# Revit family: Запорно-регулирующая заслонка с рукояткой AF-4219
name_source: partatom
category: Rohrzubehör
units: mm (PartAtom-declared; Revit-internal decimal feet)

## family parameters
Arbeitsebenenbasiert = Nein
Beim Laden mit Abzugskörper schneiden = Nein
Bemaßung runder Anschluss = Durchmesser verwenden
Gemeinsam genutzt = Nein
Immer vertikal = Ja
OmniClass-Nummer = 23.65.55.14
OmniClass-Titel = Valves for Liquid Services
Teiletyp = Unterbricht

## types (1)
- Запорно-регулирующая заслонка с рукояткой AF-4219
    Hersteller = HERZ Armaturen Ges.m.b.H.
    O-Ring = EPDM в соответствии с ISO 1691
    R99 = 2 mm  [stored 0.00656168 ft]
    SCRNCODE = 05;13;02
    SCRNSEQ = ARM;AM_TYP="ALLF";2
    SCTWCODE = 04;07;02
    SCTWSEQ = FW;SBT_TYP_FW="101";2
    URL = www.herz-armaturen.ru
    Диск = Нержавеющая сталь 1.4408
    Корпус = Чугун GGG, GJS-400-15/JS1030, в соответствии с EN1563
    Макс. рабочая температура = 110 °C
    Мин. рабочая температура = -20.00 °C при соответствующей водно-гликолевой смеси
    Область применения = Применяются в системах тепло- и холодоснабжения.
    Рукоятка DN200-DN300 = Сталь, S235 DIN2458/1626
    Рукоятка DN50-150 = Сталь, ST14.03
    Среда = Качество теплоносителя в соответствии с ÖNORM H5195 и/или предписаниями VDI 2035.
Разрешается использование смеси этилен или пропиленгликоля в соотношении 25-50% с водой.
    Уплотнение корпуса = EPDM в соответствии с ISO 1691
    Фланцевое соединение = В соответствии с EN1092-2
    Шпиндель = Нержавеющая сталь ASTM-A276 / Type 316

note: [stored X ft] marks values corroborated as IEEE doubles in the binary element streams (Revit-internal decimal feet)
